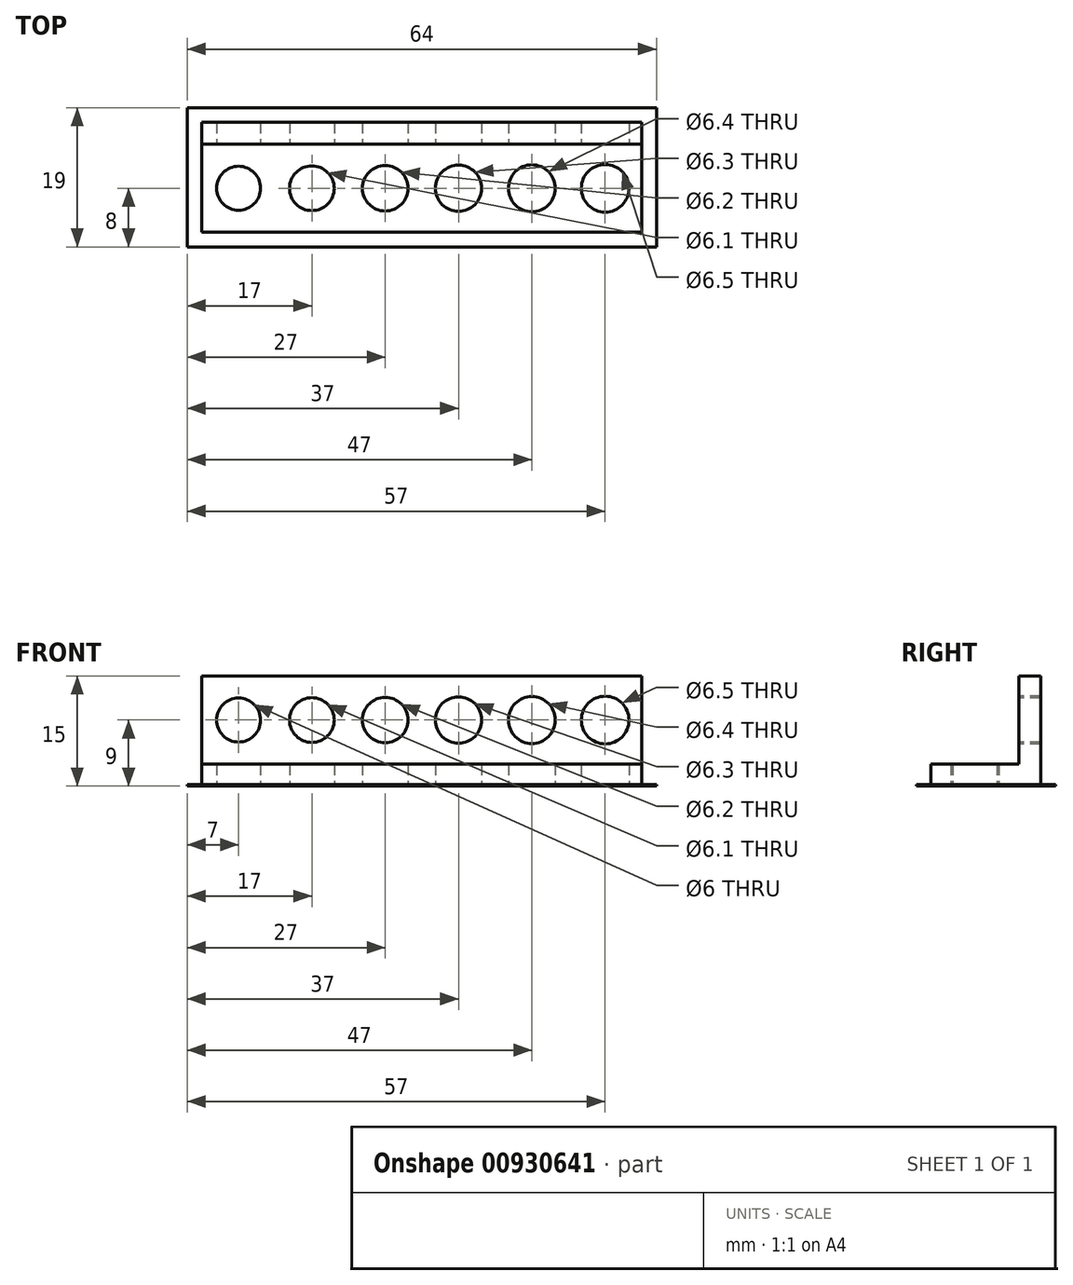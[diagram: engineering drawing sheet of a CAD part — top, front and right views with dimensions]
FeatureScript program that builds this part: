
annotation { "Feature Type Name" : "Feature", "Feature Type Description" : "" }
export const myFeature = defineFeature(function(context is Context, id is Id, definition is map)
    precondition{}
    {
        {
            var Q0;
            Q0=qCreatedBy(makeId("Top.planeOp"),FACE);
            var sketch = newSketch(context, id + "F0", { "sketchPlane" : qUnion([Q0])});
            skLineSegment(sketch, "E0.bottom", {"start": v(0, 0) * mm, "end": v(60, 0) * mm});
            skLineSegment(sketch, "E0.top", {"start": v(0, 15) * mm, "end": v(60, 15) * mm});
            skLineSegment(sketch, "E0.left", {"start": v(0, 0) * mm, "end": v(0, 15) * mm});
            skLineSegment(sketch, "E0.right", {"start": v(60, 0) * mm, "end": v(60, 15) * mm});
            skLineSegment(sketch, "E1", {"start": v(0, 6) * mm, "end": v(60, 6) * mm, "construction": true});
            skCircle(sketch, "E2", {"center": v(5, 6) * mm, "radius": 3 * mm});
            skCircle(sketch, "E3", {"center": v(15, 6) * mm, "radius": 3.05 * mm});
            skCircle(sketch, "E4", {"center": v(25, 6) * mm, "radius": 3.1 * mm});
            skCircle(sketch, "E5", {"center": v(35, 6) * mm, "radius": 3.15 * mm});
            skCircle(sketch, "E6", {"center": v(45, 6) * mm, "radius": 3.2 * mm});
            skCircle(sketch, "E7", {"center": v(55, 6) * mm, "radius": 3.25 * mm});
            skLineSegment(sketch, "E8", {"start": v(5, 15) * mm, "end": v(5, 0) * mm, "construction": true});
            skLineSegment(sketch, "E9", {"start": v(15, 15) * mm, "end": v(15, 0) * mm, "construction": true});
            skLineSegment(sketch, "E10", {"start": v(25, 15) * mm, "end": v(25, 0) * mm, "construction": true});
            skLineSegment(sketch, "E11", {"start": v(35, 15) * mm, "end": v(35, 0) * mm, "construction": true});
            skLineSegment(sketch, "E12", {"start": v(45, 15) * mm, "end": v(45, 0) * mm, "construction": true});
            skLineSegment(sketch, "E13", {"start": v(55, 15) * mm, "end": v(55, 0) * mm, "construction": true});
            skSolve(sketch);
        }
        {
            var Q0;
            Q0=qSketchRegion(id+"F0",true);
            extrude(context, id + "F1", {"entities" : qUnion([Q0]), "depth" : 3 * mm, "offsetDistance" : 25 * mm});
        }
        {
            var Q0;
            Q0=qCreatedBy(makeId("Top.planeOp"),FACE);
            var sketch = newSketch(context, id + "F2", { "sketchPlane" : qUnion([Q0])});
            skLineSegment(sketch, "E14", {"start": v(0, 0) * mm, "end": v(0, 15) * mm});
            skLineSegment(sketch, "E15", {"start": v(0, 15) * mm, "end": v(60, 15) * mm});
            skLineSegment(sketch, "E16", {"start": v(60, 15) * mm, "end": v(60, 0) * mm});
            skLineSegment(sketch, "E17", {"start": v(60, 0) * mm, "end": v(0, 0) * mm});
            skLineSegment(sketch, "E18.bottom", {"start": v(-2, 17) * mm, "end": v(62, 17) * mm});
            skLineSegment(sketch, "E18.top", {"start": v(-2, -2) * mm, "end": v(62, -2) * mm});
            skLineSegment(sketch, "E18.left", {"start": v(-2, 17) * mm, "end": v(-2, -2) * mm});
            skLineSegment(sketch, "E18.right", {"start": v(62, 17) * mm, "end": v(62, -2) * mm});
            skSolve(sketch);
        }
        {
            var Q0;
            Q0=qSketchRegion(id+"F2",true);
            extrude(context, id + "F3", {"entities" : qUnion([Q0]), "operationType" : NewBodyOperationType.ADD, "depth" : 0.2 * mm, "offsetDistance" : 25 * mm});
        }
        {
            var Q0;
            Q0=makeQuery(id+"F1.opExtrude","CAP_FACE",FACE,{"disambiguationData":[OSD([sQuery(id+"F0.wireOp",EDGE,"E0.bottom"),sQuery(id+"F0.wireOp",EDGE,"E0.top"),sQuery(id+"F0.wireOp",EDGE,"E0.left"),sQuery(id+"F0.wireOp",EDGE,"E0.right"),sQuery(id+"F0.wireOp",EDGE,"E2"),sQuery(id+"F0.wireOp",EDGE,"E3"),sQuery(id+"F0.wireOp",EDGE,"E4"),sQuery(id+"F0.wireOp",EDGE,"E5"),sQuery(id+"F0.wireOp",EDGE,"E6"),sQuery(id+"F0.wireOp",EDGE,"E7")])],"isStart":false});
            var sketch = newSketch(context, id + "F4", { "sketchPlane" : qUnion([Q0])});
            skLineSegment(sketch, "E19.bottom", {"start": v(0, 15) * mm, "end": v(60, 15) * mm});
            skLineSegment(sketch, "E19.top", {"start": v(0, 12) * mm, "end": v(60, 12) * mm});
            skLineSegment(sketch, "E19.left", {"start": v(0, 15) * mm, "end": v(0, 12) * mm});
            skLineSegment(sketch, "E19.right", {"start": v(60, 15) * mm, "end": v(60, 12) * mm});
            skSolve(sketch);
        }
        {
            var Q0;
            Q0=qSketchRegion(id+"F4",true);
            extrude(context, id + "F5", {"entities" : qUnion([Q0]), "operationType" : NewBodyOperationType.ADD, "depth" : 12 * mm, "offsetDistance" : 25 * mm});
        }
        {
            var Q0;
            Q0=makeQuery(id+"F5.opExtrude","SWEPT_FACE",FACE,{"disambiguationData":[OSD([sQuery(id+"F4.wireOp",EDGE,"E19.top")])]});
            var sketch = newSketch(context, id + "F6", { "sketchPlane" : qUnion([Q0])});
            skLineSegment(sketch, "E20", {"start": v(0, 9) * mm, "end": v(60, 9) * mm, "construction": true});
            skLineSegment(sketch, "E21", {"start": v(5, 15) * mm, "end": v(5, 3) * mm, "construction": true});
            skLineSegment(sketch, "E22", {"start": v(15, 15) * mm, "end": v(15, 3) * mm, "construction": true});
            skLineSegment(sketch, "E23", {"start": v(25, 15) * mm, "end": v(25, 3) * mm, "construction": true});
            skLineSegment(sketch, "E24", {"start": v(35, 15) * mm, "end": v(35, 3) * mm, "construction": true});
            skLineSegment(sketch, "E25", {"start": v(45, 15) * mm, "end": v(45, 3) * mm, "construction": true});
            skLineSegment(sketch, "E26", {"start": v(55, 15) * mm, "end": v(55, 3) * mm, "construction": true});
            skCircle(sketch, "E27", {"center": v(5, 9) * mm, "radius": 3 * mm});
            skCircle(sketch, "E28", {"center": v(15, 9) * mm, "radius": 3.05 * mm});
            skCircle(sketch, "E29", {"center": v(25, 9) * mm, "radius": 3.1 * mm});
            skCircle(sketch, "E30", {"center": v(35, 9) * mm, "radius": 3.15 * mm});
            skCircle(sketch, "E31", {"center": v(45, 9) * mm, "radius": 3.2 * mm});
            skCircle(sketch, "E32", {"center": v(55, 9) * mm, "radius": 3.25 * mm});
            skSolve(sketch);
        }
        {
            var Q0;
            Q0=qSketchRegion(id+"F6",true);
            extrude(context, id + "F7", {"entities" : qUnion([Q0]), "operationType" : NewBodyOperationType.REMOVE, "endBound" : BoundingType.UP_TO_NEXT, "oppositeDirection" : true, "depth" : 25 * mm, "offsetDistance" : 25 * mm});
        }
    });
